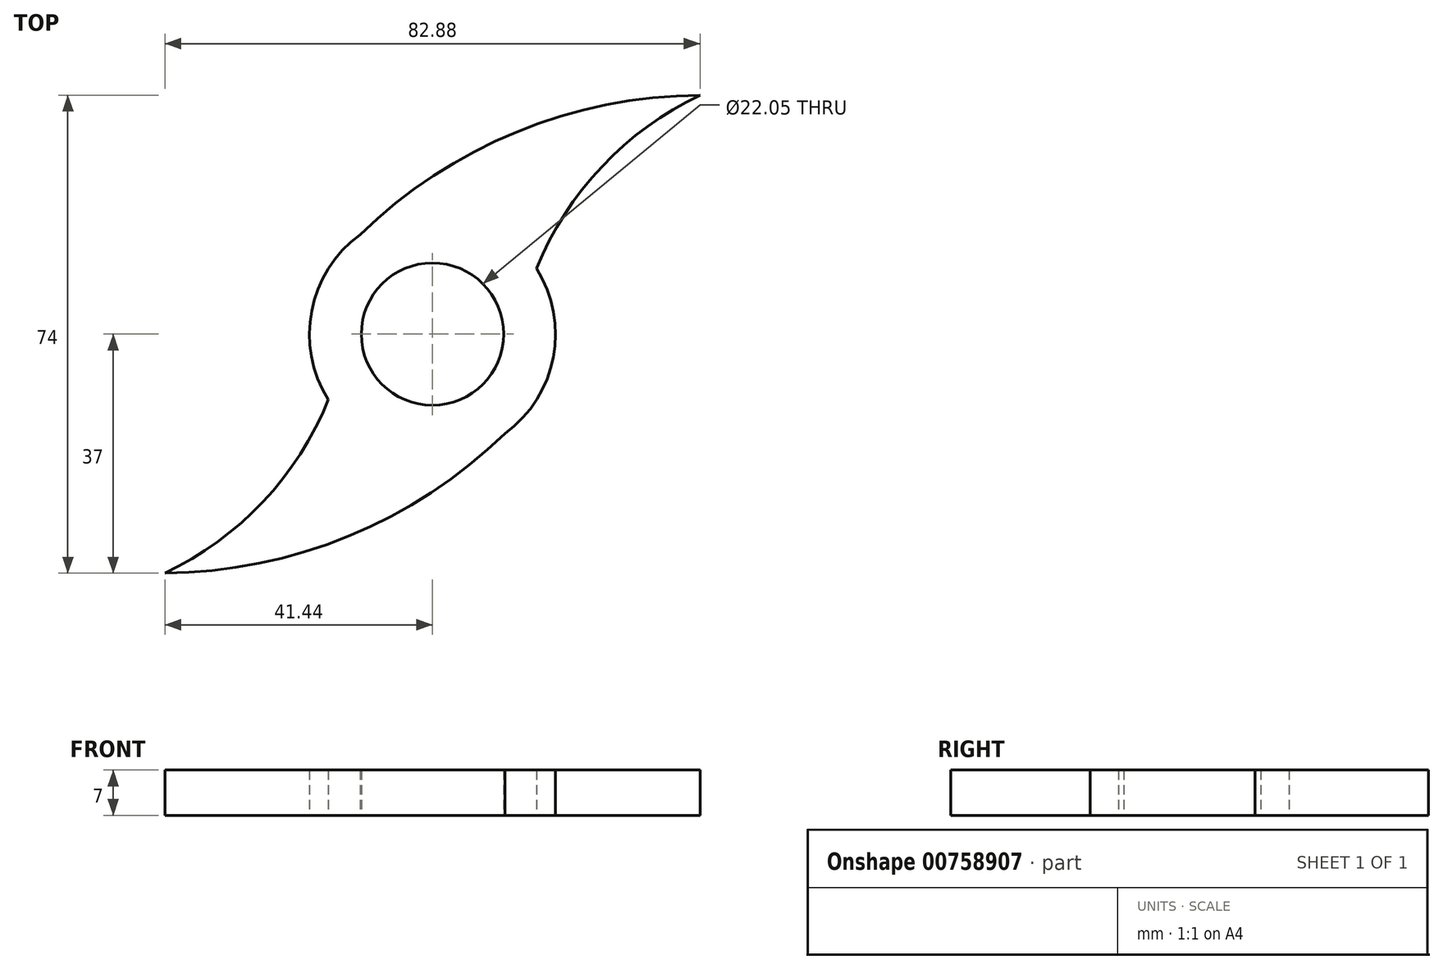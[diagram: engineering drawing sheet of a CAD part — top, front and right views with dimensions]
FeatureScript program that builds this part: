
annotation { "Feature Type Name" : "Feature", "Feature Type Description" : "" }
export const myFeature = defineFeature(function(context is Context, id is Id, definition is map)
    precondition{}
    {
        {
            var Q0;
            Q0=qCreatedBy(makeId("Top.planeOp"),FACE);
            var sketch = newSketch(context, id + "F0", { "sketchPlane" : qUnion([Q0])});
            skEllipse(sketch, "E0", {"center": v(0, 0) * mm, "majorRadius": 33.02 * mm, "minorRadius": 19.05 * mm, "majorAxis": v(1, 0), "construction": true});
            skCircle(sketch, "E1", {"center": v(0, 0) * mm, "radius": 11.03 * mm});
            skLineSegment(sketch, "E2", {"start": v(-33.02, 0) * mm, "end": v(33.02, 0) * mm, "construction": true});
            skLineSegment(sketch, "E3", {"start": v(0, 19.05) * mm, "end": v(0, -19.05) * mm, "construction": true});
            skCircle(sketch, "E4", {"center": v(0, 0) * mm, "radius": 19.05 * mm});
            skLineSegment(sketch, "E5", {"start": v(-16.11, 10.16) * mm, "end": v(16.11, 10.16) * mm, "construction": true});
            skLineSegment(sketch, "E6", {"start": v(-16.11, 10.16) * mm, "end": v(41.44, 37) * mm, "construction": true});
            skLineSegment(sketch, "E7", {"start": v(16.11, 10.16) * mm, "end": v(41.44, 37) * mm, "construction": true});
            skArc(sketch, "E8", {"start": v(41.44, 37) * mm, "mid": v(26.25, 25.96) * mm, "end": v(16.11, 10.16) * mm});
            skArc(sketch, "E9", {"start": v(41.44, 37) * mm, "mid": v(9.73, 29.86) * mm, "end": v(-16.11, 10.16) * mm});
            skArc(sketch, "E10.1.0", {"start": v(-41.44, -37) * mm, "mid": v(-9.73, -29.86) * mm, "end": v(16.11, -10.16) * mm});
            skArc(sketch, "E10.1.1", {"start": v(-41.44, -37) * mm, "mid": v(-26.25, -25.96) * mm, "end": v(-16.11, -10.16) * mm});
            skSolve(sketch);
        }
        {
            var Q0;
            Q0=makeQuery(id+"F0.imprint","IMPRINT",FACE,{"disambiguationData":[TD([[makeQuery(id+"F0.imprint","IMPRINT",EDGE,{"derivedFrom":sQuery(id+"F0.wireOp",EDGE,"E1")}),-1.0]])]});
            var Q1;
            {var subQ0=sQuery(id+"F0.wireOp",EDGE,"E8");Q1=makeQuery(id+"F0.imprint","IMPRINT",FACE,{"disambiguationData":[TD([[makeQuery(id+"F0.imprint","IMPRINT",EDGE,{"derivedFrom":subQ0}),-1.0]])]});}
            var Q2;
            {var subQ0=sQuery(id+"F0.wireOp",EDGE,"E10.1.1");Q2=makeQuery(id+"F0.imprint","IMPRINT",FACE,{"disambiguationData":[TD([[makeQuery(id+"F0.imprint","IMPRINT",EDGE,{"derivedFrom":subQ0}),-1.0]])]});}
            var Q3;
            {var subQ0=sQuery(id+"F0.wireOp",EDGE,"E9");var subQ1=sQuery(id+"F0.wireOp",EDGE,"E4");var subQ2=makeQuery(id+"F0.imprint","INTERSECT",VERTEX,{"disambiguationData":[OD(0.0)],"derivedFrom":[subQ1,subQ0]});Q3=makeQuery(id+"F0.imprint","IMPRINT",FACE,{"disambiguationData":[TD([[makeQuery(id+"F0.imprint","IMPRINT",EDGE,{"disambiguationData":[TD([[subQ2,1.0]])],"derivedFrom":subQ1}),1.0]])]});}
            var Q4;
            {var subQ0=sQuery(id+"F0.wireOp",EDGE,"E10.1.0");var subQ1=sQuery(id+"F0.wireOp",EDGE,"E4");var subQ2=makeQuery(id+"F0.imprint","INTERSECT",VERTEX,{"disambiguationData":[OD(0.0)],"derivedFrom":[subQ1,subQ0]});Q4=makeQuery(id+"F0.imprint","IMPRINT",FACE,{"disambiguationData":[TD([[makeQuery(id+"F0.imprint","IMPRINT",EDGE,{"disambiguationData":[TD([[subQ2,1.0]])],"derivedFrom":subQ1}),1.0]])]});}
            extrude(context, id + "F1", {"entities" : qUnion([Q0, Q1, Q2, Q3, Q4]), "depth" : 7 * mm, "offsetDistance" : 25.4 * mm});
        }
    });
